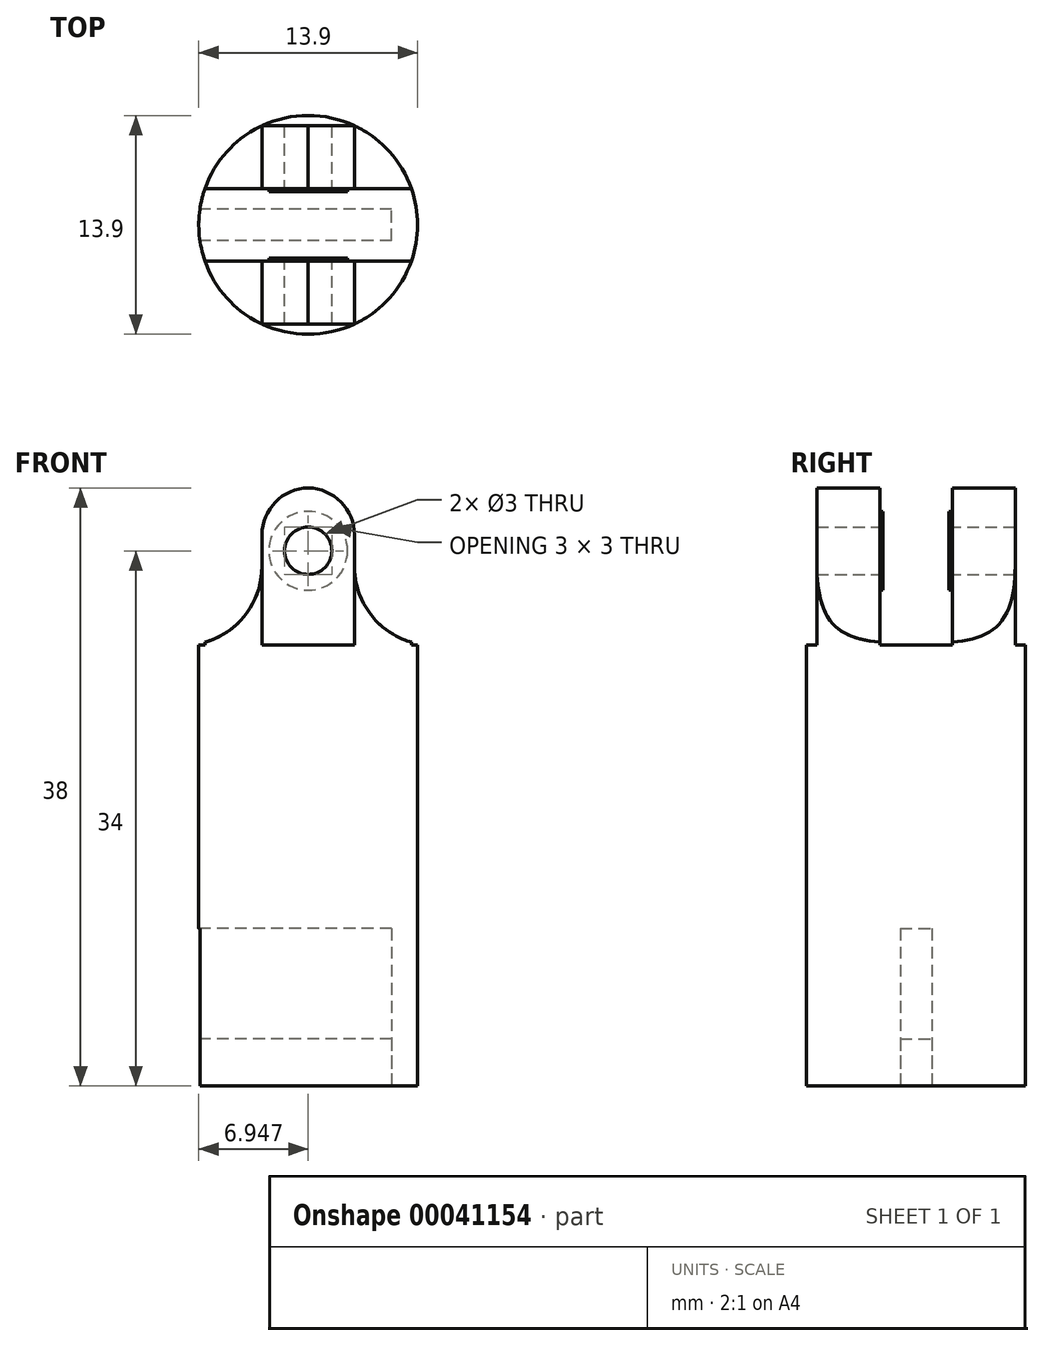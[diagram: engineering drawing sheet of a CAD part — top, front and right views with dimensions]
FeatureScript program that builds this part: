
annotation { "Feature Type Name" : "Feature", "Feature Type Description" : "" }
export const myFeature = defineFeature(function(context is Context, id is Id, definition is map)
    precondition{}
    {
        {
            var Q0;
            Q0=qCreatedBy(makeId("Top.planeOp"),FACE);
            var sketch = newSketch(context, id + "F0", { "sketchPlane" : qUnion([Q0])});
            skLineSegment(sketch, "E0", {"start": v(0, -0.07) * mm, "end": v(-0.27, -0.07) * mm});
            skPoint(sketch, "E1.visualSharp", {"position": v(-9.62, 20.9) * mm});
            skCircle(sketch, "E2", {"center": v(-16.02, 6.95) * mm, "radius": 6.95 * mm});
            skSolve(sketch);
        }
        {
            var Q0;
            Q0=qSketchRegion(id+"F0",true);
            extrude(context, id + "F1", {"entities" : qUnion([Q0]), "depth" : 28 * mm});
        }
        {
            var Q0;
            Q0=makeQuery(id+"F1.opExtrude","CAP_FACE",FACE,{"disambiguationData":[OSD([sQuery(id+"F0.wireOp",EDGE,"E2")])],"isStart":false});
            var sketch = newSketch(context, id + "F2", { "sketchPlane" : qUnion([Q0])});
            skLineSegment(sketch, "E3", {"start": v(-16.02, 6.95) * mm, "end": v(-9.07, 6.95) * mm});
            skLineSegment(sketch, "E4", {"start": v(-16.02, 6.95) * mm, "end": v(-22.97, 6.95) * mm});
            skLineSegment(sketch, "E5", {"start": v(-22.58, 4.65) * mm, "end": v(-9.47, 4.65) * mm});
            skLineSegment(sketch, "E6", {"start": v(-9.47, 9.25) * mm, "end": v(-22.58, 9.25) * mm});
            skLineSegment(sketch, "E7", {"start": v(-16.02, 6.95) * mm, "end": v(-16.02, 0) * mm});
            skLineSegment(sketch, "E8", {"start": v(-13.09, 0.65) * mm, "end": v(-18.96, 0.65) * mm});
            skLineSegment(sketch, "E9", {"start": v(-13.09, 13.25) * mm, "end": v(-18.96, 13.25) * mm});
            skLineSegment(sketch, "E10", {"start": v(-16.02, 6.95) * mm, "end": v(-16.02, 13.25) * mm});
            skLineSegment(sketch, "E11", {"start": v(-13.09, 13.25) * mm, "end": v(-13.09, 9.25) * mm});
            skLineSegment(sketch, "E12", {"start": v(-13.09, 0.65) * mm, "end": v(-13.09, 4.65) * mm});
            skLineSegment(sketch, "E13", {"start": v(-18.96, 0.65) * mm, "end": v(-18.96, 4.65) * mm});
            skLineSegment(sketch, "E14", {"start": v(-18.96, 13.25) * mm, "end": v(-18.96, 9.25) * mm});
            skSolve(sketch);
        }
        {
            var Q0;
            Q0=qSketchRegion(id+"F2",true);
            extrude(context, id + "F3", {"entities" : qUnion([Q0]), "operationType" : NewBodyOperationType.ADD, "depth" : 10 * mm});
        }
        {
            var Q0;
            Q0=makeQuery(id+"F3.opExtrude","CAP_EDGE",EDGE,{"disambiguationData":[OSD([sQuery(id+"F2.wireOp",EDGE,"E12")])],"isStart":false});
            var Q1;
            Q1=makeQuery(id+"F3.opExtrude","CAP_EDGE",EDGE,{"disambiguationData":[OSD([sQuery(id+"F2.wireOp",EDGE,"E11")])],"isStart":false});
            var Q2;
            Q2=makeQuery(id+"F3.opExtrude","CAP_EDGE",EDGE,{"disambiguationData":[OSD([sQuery(id+"F2.wireOp",EDGE,"E14")])],"isStart":false});
            var Q3;
            Q3=makeQuery(id+"F3.opExtrude","CAP_EDGE",EDGE,{"disambiguationData":[OSD([sQuery(id+"F2.wireOp",EDGE,"E13")])],"isStart":false});
            fillet(context, id + "F4", {"entities" : qUnion([Q0, Q1, Q2, Q3]), "radius" : 3 * mm, "tangentPropagation" : true, "allowEdgeOverflow" : false});
        }
        {
            var Q0;
            Q0=makeQuery(id+"F3.opExtrude","CAP_EDGE",EDGE,{"disambiguationData":[OSD([sQuery(id+"F2.wireOp",EDGE,"E12")])],"isStart":true});
            var Q1;
            Q1=makeQuery(id+"F3.opExtrude","CAP_EDGE",EDGE,{"disambiguationData":[OSD([sQuery(id+"F2.wireOp",EDGE,"E11")])],"isStart":true});
            var Q2;
            Q2=makeQuery(id+"F3.opExtrude","CAP_EDGE",EDGE,{"disambiguationData":[OSD([sQuery(id+"F2.wireOp",EDGE,"E14")])],"isStart":true});
            var Q3;
            Q3=makeQuery(id+"F3.opExtrude","CAP_EDGE",EDGE,{"disambiguationData":[OSD([sQuery(id+"F2.wireOp",EDGE,"E13")])],"isStart":true});
            fillet(context, id + "F5", {"entities" : qUnion([Q0, Q1, Q2, Q3]), "radius" : 5 * mm, "tangentPropagation" : true, "allowEdgeOverflow" : false});
        }
        {
            var Q0;
            Q0=makeQuery(id+"F3.opExtrude","SWEPT_FACE",FACE,{"disambiguationData":[OSD([sQuery(id+"F2.wireOp",EDGE,"E9")])]});
            var sketch = newSketch(context, id + "F6", { "sketchPlane" : qUnion([Q0])});
            skLineSegment(sketch, "E15", {"start": v(13.09, 34) * mm, "end": v(18.96, 34) * mm});
            skCircle(sketch, "E16", {"center": v(16.02, 34) * mm, "radius": 1.5 * mm});
            skSolve(sketch);
        }
        {
            var Q0;
            Q0=makeQuery(id+"F1.opExtrude","CAP_FACE",FACE,{"disambiguationData":[OSD([sQuery(id+"F0.wireOp",EDGE,"E2")])],"isStart":true});
            var sketch = newSketch(context, id + "F7", { "sketchPlane" : qUnion([Q0])});
            skLineSegment(sketch, "E17", {"start": v(-10.73, -5.95) * mm, "end": v(-10.73, -7.95) * mm});
            skLineSegment(sketch, "E18", {"start": v(-10.73, -5.95) * mm, "end": v(-23.31, -5.95) * mm});
            skLineSegment(sketch, "E19", {"start": v(-10.73, -7.95) * mm, "end": v(-23.31, -7.95) * mm});
            skLineSegment(sketch, "E20", {"start": v(-23.31, -7.95) * mm, "end": v(-23.31, -5.95) * mm});
            skSolve(sketch);
        }
        {
            var Q0;
            Q0=qSketchRegion(id+"F7",true);
            extrude(context, id + "F8", {"entities" : qUnion([Q0]), "operationType" : NewBodyOperationType.REMOVE, "oppositeDirection" : true, "depth" : 10 * mm});
        }
        {
            var Q0;
            Q0=makeQuery(id+"F1.opExtrude","CAP_FACE",FACE,{"disambiguationData":[OSD([sQuery(id+"F0.wireOp",EDGE,"E2")])],"isStart":true});
            var sketch = newSketch(context, id + "F9", { "sketchPlane" : qUnion([Q0])});
            skLineSegment(sketch, "E21", {"start": v(-22.9, -5.95) * mm, "end": v(-22.9, -7.95) * mm});
            skLineSegment(sketch, "E22", {"start": v(-22.9, -7.95) * mm, "end": v(-10.73, -7.95) * mm});
            skLineSegment(sketch, "E23", {"start": v(-10.73, -7.95) * mm, "end": v(-10.73, -5.95) * mm});
            skLineSegment(sketch, "E24", {"start": v(-10.73, -5.95) * mm, "end": v(-22.9, -5.95) * mm});
            skSolve(sketch);
        }
        {
            var Q0;
            Q0=qSketchRegion(id+"F9",true);
            extrude(context, id + "F10", {"entities" : qUnion([Q0]), "oppositeDirection" : true, "depth" : 3 * mm});
        }
        {
            var Q0;
            Q0=makeQuery(id+"F3.opExtrude","SWEPT_FACE",FACE,{"disambiguationData":[OSD([sQuery(id+"F2.wireOp",EDGE,"E5")])]});
            var sketch = newSketch(context, id + "F11", { "sketchPlane" : qUnion([Q0])});
            skCircle(sketch, "E25", {"center": v(16.02, 34) * mm, "radius": 2.5 * mm});
            skSolve(sketch);
        }
        {
            var Q0;
            Q0=qSketchRegion(id+"F11",true);
            extrude(context, id + "F12", {"entities" : qUnion([Q0]), "operationType" : NewBodyOperationType.ADD, "depth" : 0.2 * mm});
        }
        {
            var Q0;
            Q0=makeQuery(id+"F3.opExtrude","SWEPT_FACE",FACE,{"disambiguationData":[OSD([sQuery(id+"F2.wireOp",EDGE,"E6")])]});
            var sketch = newSketch(context, id + "F13", { "sketchPlane" : qUnion([Q0])});
            skCircle(sketch, "E26", {"center": v(-16.02, 34) * mm, "radius": 2.5 * mm});
            skSolve(sketch);
        }
        {
            var Q0;
            Q0=qSketchRegion(id+"F13",true);
            extrude(context, id + "F14", {"entities" : qUnion([Q0]), "operationType" : NewBodyOperationType.ADD, "depth" : 0.2 * mm});
        }
        {
            var Q0;
            Q0=qSketchRegion(id+"F6",true);
            extrude(context, id + "F15", {"entities" : qUnion([Q0]), "operationType" : NewBodyOperationType.REMOVE, "endBound" : BoundingType.THROUGH_ALL, "oppositeDirection" : true, "depth" : 25 * mm});
        }
    });
